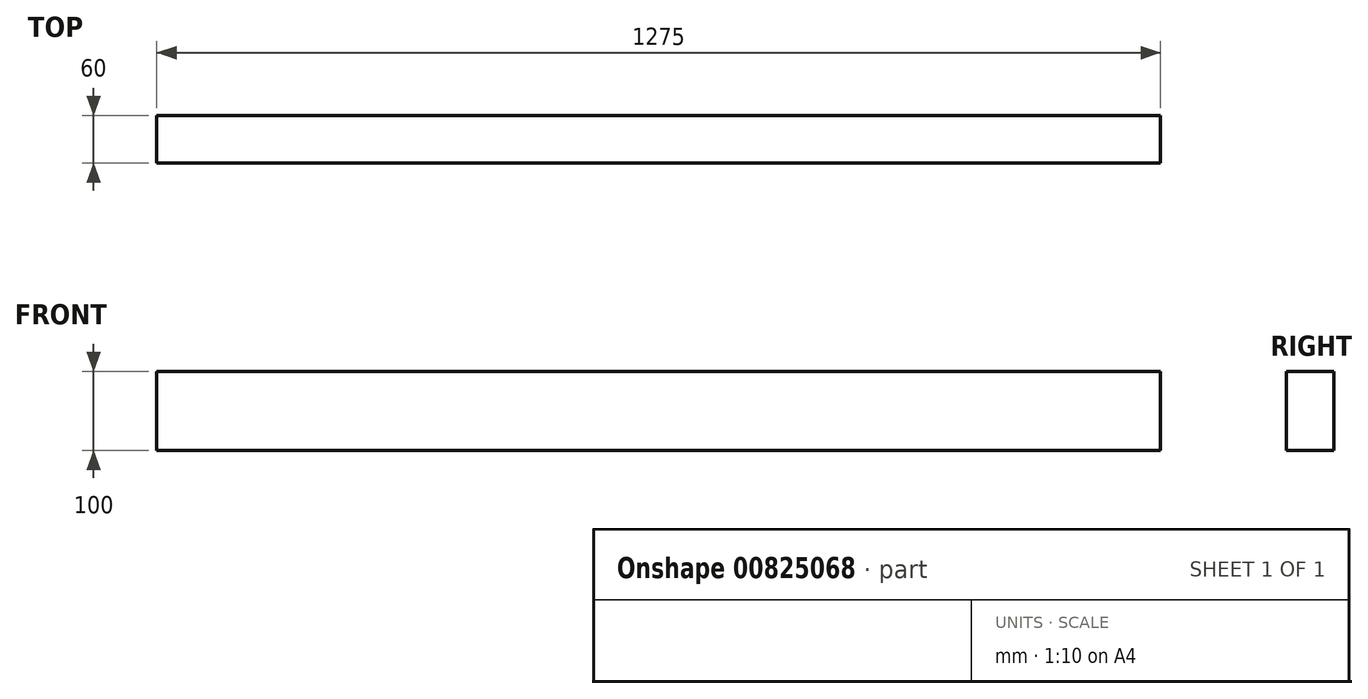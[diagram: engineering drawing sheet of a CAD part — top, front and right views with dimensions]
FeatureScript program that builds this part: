
annotation { "Feature Type Name" : "Feature", "Feature Type Description" : "" }
export const myFeature = defineFeature(function(context is Context, id is Id, definition is map)
    precondition{}
    {
        {
            var Q0;
            Q0=qCreatedBy(makeId("Top.planeOp"),FACE);
            var sketch = newSketch(context, id + "F0", { "sketchPlane" : qUnion([Q0])});
            skLineSegment(sketch, "E0.bottom", {"start": v(-790.31, 64.32) * mm, "end": v(484.69, 64.32) * mm});
            skLineSegment(sketch, "E0.top", {"start": v(-790.31, 4.32) * mm, "end": v(484.69, 4.32) * mm});
            skLineSegment(sketch, "E0.left", {"start": v(-790.31, 64.32) * mm, "end": v(-790.31, 4.32) * mm});
            skLineSegment(sketch, "E0.right", {"start": v(484.69, 64.32) * mm, "end": v(484.69, 4.32) * mm});
            skSolve(sketch);
        }
        {
            var Q0;
            Q0 = qSketchRegion(id + "F0", true);
            extrude(context, id + "F1", {"entities" : qUnion([Q0]), "depth" : 100 * mm, "offsetDistance" : 25 * mm});
        }
    });
